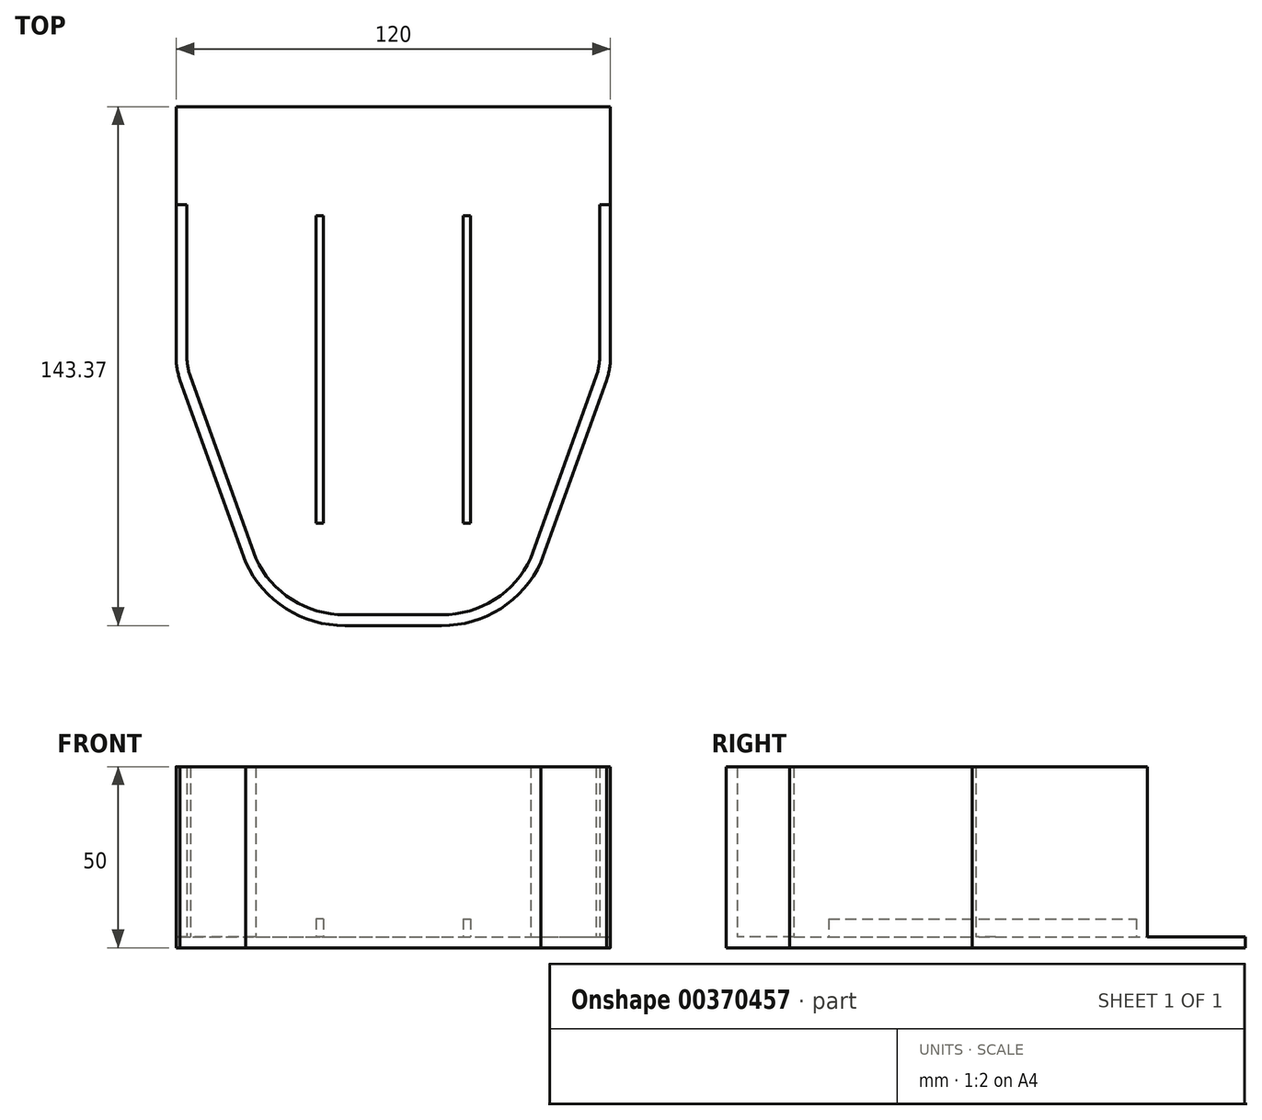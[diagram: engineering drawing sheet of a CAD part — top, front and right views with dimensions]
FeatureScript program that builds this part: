
annotation { "Feature Type Name" : "Feature", "Feature Type Description" : "" }
export const myFeature = defineFeature(function(context is Context, id is Id, definition is map)
    precondition{}
    {
        {
            var Q0;
            Q0=qCreatedBy(makeId("Top.planeOp"),FACE);
            var sketch = newSketch(context, id + "F0", { "sketchPlane" : qUnion([Q0])});
            skLineSegment(sketch, "E0", {"start": v(10.86, -56.16) * mm, "end": v(-15.84, -56.16) * mm});
            skLineSegment(sketch, "E1", {"start": v(-43.3, -38.66) * mm, "end": v(-61.38, 11.69) * mm});
            skLineSegment(sketch, "E2", {"start": v(-62.5, 18.26) * mm, "end": v(-62.5, 40.2) * mm});
            skArc(sketch, "E3", {"start": v(-43.3, -38.66) * mm, "mid": v(-32.15, -51.46) * mm, "end": v(-15.84, -56.16) * mm});
            skArc(sketch, "E4", {"start": v(-62.5, 18.26) * mm, "mid": v(-62.21, 14.93) * mm, "end": v(-61.38, 11.69) * mm});
            skLineSegment(sketch, "E5", {"start": v(-2.5, 108.98) * mm, "end": v(-2.5, -99.64) * mm, "construction": true});
            skPoint(sketch, "E5.endSnap0", {"position": v(-2.5, -56.16) * mm});
            skLineSegment(sketch, "E6.MirrorCS", {"start": v(-15.84, -56.16) * mm, "end": v(10.86, -56.16) * mm});
            skArc(sketch, "E7.MirrorCS", {"start": v(38.31, -38.66) * mm, "mid": v(27.17, -51.46) * mm, "end": v(10.86, -56.16) * mm});
            skLineSegment(sketch, "E8.MirrorCS", {"start": v(38.31, -38.66) * mm, "end": v(56.4, 11.69) * mm});
            skArc(sketch, "E9.MirrorCS", {"start": v(57.5, 18.26) * mm, "mid": v(57.23, 14.93) * mm, "end": v(56.4, 11.69) * mm});
            skLineSegment(sketch, "E10.MirrorCS", {"start": v(57.5, 18.26) * mm, "end": v(57.5, 40.2) * mm});
            skLineSegment(sketch, "E11", {"start": v(-62.5, 40.2) * mm, "end": v(-62.5, 90.2) * mm});
            skLineSegment(sketch, "E12.MirrorCS", {"start": v(57.5, 40.2) * mm, "end": v(57.5, 90.2) * mm});
            skLineSegment(sketch, "E13", {"start": v(-62.5, 90.2) * mm, "end": v(57.5, 90.2) * mm});
            skLineSegment(sketch, "E14.bottom", {"start": v(-21.85, -27.88) * mm, "end": v(-23.85, -27.88) * mm});
            skLineSegment(sketch, "E14.top", {"start": v(-21.85, 57.12) * mm, "end": v(-23.85, 57.12) * mm});
            skLineSegment(sketch, "E14.left", {"start": v(-21.85, -27.88) * mm, "end": v(-21.85, 57.12) * mm});
            skLineSegment(sketch, "E14.right", {"start": v(-23.85, -27.88) * mm, "end": v(-23.85, 57.12) * mm});
            skLineSegment(sketch, "E15.bottom", {"start": v(16.86, 57.12) * mm, "end": v(18.86, 57.12) * mm});
            skLineSegment(sketch, "E15.top", {"start": v(16.86, -27.88) * mm, "end": v(18.86, -27.88) * mm});
            skLineSegment(sketch, "E15.left", {"start": v(18.86, 57.12) * mm, "end": v(18.86, -27.88) * mm});
            skLineSegment(sketch, "E15.right", {"start": v(16.86, 57.12) * mm, "end": v(16.86, -27.88) * mm});
            skLineSegment(sketch, "E16", {"start": v(57.5, 18.26) * mm, "end": v(-62.5, 18.26) * mm, "construction": true});
            skLineSegment(sketch, "E17.0", {"start": v(-59.5, 40.55) * mm, "end": v(-59.5, 87.2) * mm});
            skLineSegment(sketch, "E17.1", {"start": v(35.53, -37.52) * mm, "end": v(53.57, 12.69) * mm});
            skArc(sketch, "E17.2", {"start": v(54.5, 18.26) * mm, "mid": v(54.27, 15.43) * mm, "end": v(53.57, 12.69) * mm});
            skLineSegment(sketch, "E17.3", {"start": v(54.5, 18.26) * mm, "end": v(54.5, 40.55) * mm});
            skLineSegment(sketch, "E17.4", {"start": v(54.5, 40.55) * mm, "end": v(54.5, 87.2) * mm});
            skArc(sketch, "E17.5", {"start": v(35.53, -37.52) * mm, "mid": v(25.5, -48.96) * mm, "end": v(10.87, -53.16) * mm});
            skLineSegment(sketch, "E17.6", {"start": v(-59.5, 87.2) * mm, "end": v(54.5, 87.2) * mm});
            skLineSegment(sketch, "E17.7", {"start": v(-15.84, -53.16) * mm, "end": v(10.87, -53.16) * mm});
            skArc(sketch, "E17.8", {"start": v(-40.51, -37.52) * mm, "mid": v(-30.48, -48.96) * mm, "end": v(-15.84, -53.16) * mm});
            skLineSegment(sketch, "E17.9", {"start": v(-40.51, -37.52) * mm, "end": v(-58.55, 12.69) * mm});
            skArc(sketch, "E17.10", {"start": v(-59.5, 18.26) * mm, "mid": v(-59.25, 15.43) * mm, "end": v(-58.55, 12.69) * mm});
            skLineSegment(sketch, "E17.11", {"start": v(-59.5, 18.26) * mm, "end": v(-59.5, 40.55) * mm});
            skLineSegment(sketch, "E18", {"start": v(54.5, 87.2) * mm, "end": v(57.5, 87.2) * mm});
            skLineSegment(sketch, "E19", {"start": v(-59.5, 87.2) * mm, "end": v(-62.5, 87.2) * mm});
            skLineSegment(sketch, "E20", {"start": v(54.5, 60.1) * mm, "end": v(57.5, 60.1) * mm});
            skLineSegment(sketch, "E21.MirrorCS", {"start": v(-59.5, 60.1) * mm, "end": v(-62.5, 60.1) * mm});
            skSolve(sketch);
        }
        {
            var Q0;
            Q0=makeQuery(id+"F0.imprint","IMPRINT",FACE,{"disambiguationData":[TD([[makeQuery(id+"F0.imprint","IMPRINT",EDGE,{"derivedFrom":sQuery(id+"F0.wireOp",EDGE,"E14.bottom")}),1.0]])]});
            var Q1;
            {var subQ0=sQuery(id+"F0.wireOp",EDGE,"E19");Q1=makeQuery(id+"F0.imprint","IMPRINT",FACE,{"disambiguationData":[TD([[makeQuery(id+"F0.imprint","IMPRINT",EDGE,{"derivedFrom":subQ0}),1.0]])]});}
            var Q2;
            {var subQ0=sQuery(id+"F0.wireOp",EDGE,"E18");Q2=makeQuery(id+"F0.imprint","IMPRINT",FACE,{"disambiguationData":[TD([[makeQuery(id+"F0.imprint","IMPRINT",EDGE,{"derivedFrom":subQ0}),-1.0]])]});}
            extrude(context, id + "F1", {"entities" : qUnion([Q0, Q1, Q2]), "depth" : 3 * mm});
        }
        {
            var Q0;
            Q0=makeQuery(id+"F0.imprint","IMPRINT",FACE,{"disambiguationData":[TD([[makeQuery(id+"F0.imprint","IMPRINT",EDGE,{"derivedFrom":sQuery(id+"F0.wireOp",EDGE,"E1")}),-1.0]])]});
            extrude(context, id + "F2", {"entities" : qUnion([Q0]), "operationType" : NewBodyOperationType.ADD, "depth" : 50 * mm});
        }
        {
            var Q0;
            Q0=makeQuery(id+"F0.imprint","IMPRINT",FACE,{"disambiguationData":[TD([[makeQuery(id+"F0.imprint","IMPRINT",EDGE,{"derivedFrom":sQuery(id+"F0.wireOp",EDGE,"E15.bottom")}),-1.0]])]});
            var Q1;
            Q1=makeQuery(id+"F0.imprint","IMPRINT",FACE,{"disambiguationData":[TD([[makeQuery(id+"F0.imprint","IMPRINT",EDGE,{"derivedFrom":sQuery(id+"F0.wireOp",EDGE,"E14.bottom")}),-1.0]])]});
            extrude(context, id + "F3", {"entities" : qUnion([Q0, Q1]), "operationType" : NewBodyOperationType.ADD, "depth" : 8 * mm});
        }
    });
